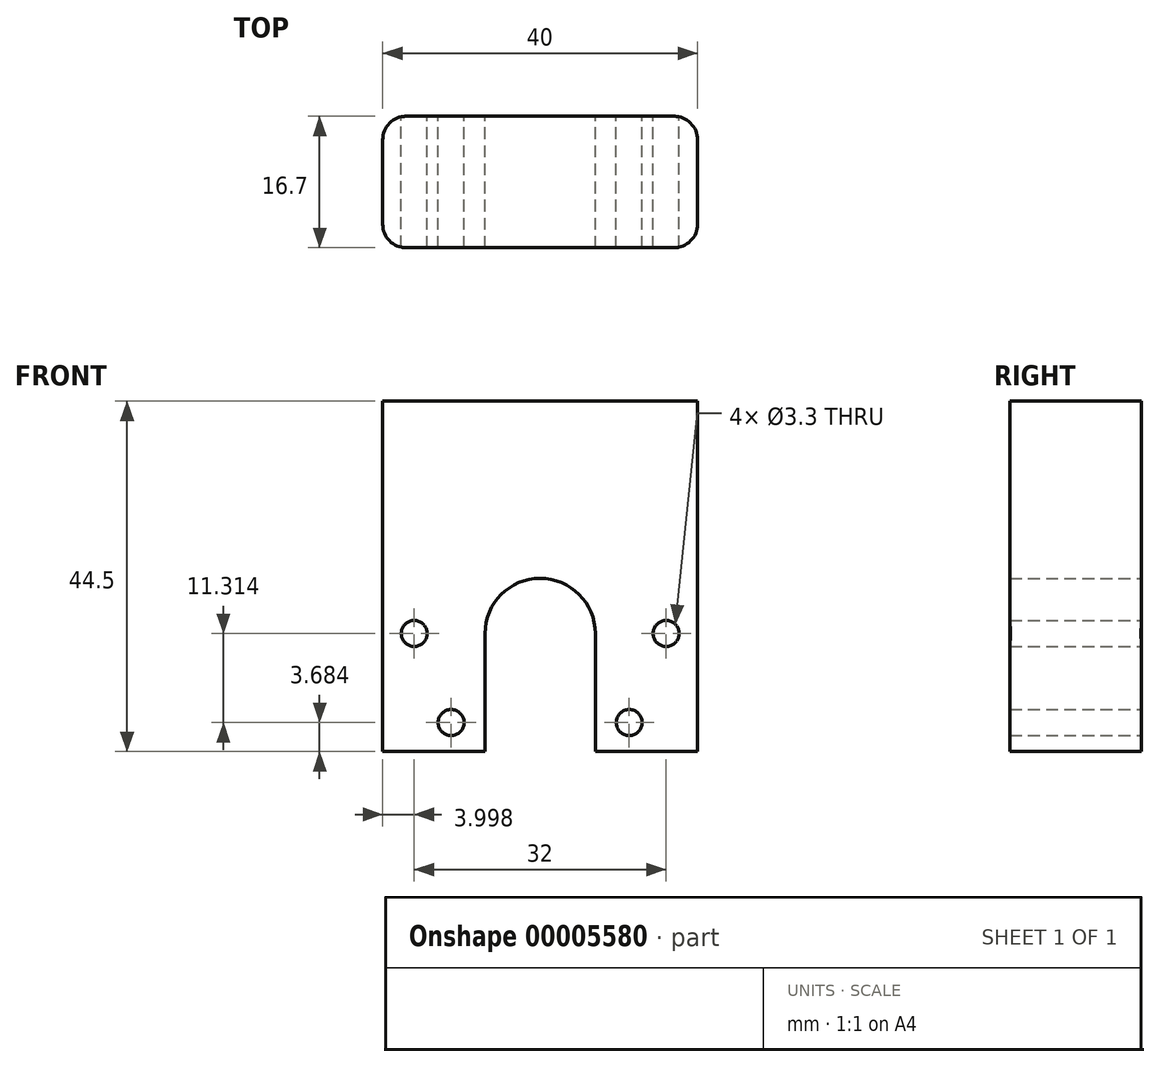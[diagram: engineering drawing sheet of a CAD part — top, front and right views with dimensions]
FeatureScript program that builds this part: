
annotation { "Feature Type Name" : "Feature", "Feature Type Description" : "" }
export const myFeature = defineFeature(function(context is Context, id is Id, definition is map)
    precondition{}
    {
        {
            var Q0;
            Q0=qCreatedBy(makeId("Front.planeOp"),FACE);
            var sketch = newSketch(context, id + "F0", { "sketchPlane" : qUnion([Q0])});
            skLineSegment(sketch, "E0.bottom", {"start": v(-19.28, 16.73) * mm, "end": v(20.72, 16.73) * mm});
            skLineSegment(sketch, "E0.top", {"start": v(-19.28, -27.77) * mm, "end": v(-6.28, -27.77) * mm});
            skLineSegment(sketch, "E0.left", {"start": v(-19.28, 16.73) * mm, "end": v(-19.28, -27.77) * mm});
            skLineSegment(sketch, "E0.right", {"start": v(20.72, 16.73) * mm, "end": v(20.72, -27.77) * mm});
            skLineSegment(sketch, "E1", {"start": v(0.72, 16.73) * mm, "end": v(0.72, -27.77) * mm, "construction": true});
            skLineSegment(sketch, "E2", {"start": v(0.72, -12.77) * mm, "end": v(-15.28, -12.77) * mm, "construction": true});
            skCircle(sketch, "E3", {"center": v(-15.28, -12.77) * mm, "radius": 1.65 * mm});
            skCircle(sketch, "E4.0.MirrorC", {"center": v(16.72, -12.77) * mm, "radius": 1.65 * mm});
            skArc(sketch, "E5", {"start": v(7.72, -12.77) * mm, "mid": v(0.72, -5.77) * mm, "end": v(-6.28, -12.77) * mm});
            skLineSegment(sketch, "E6", {"start": v(-6.28, -12.77) * mm, "end": v(-6.28, -27.77) * mm});
            skLineSegment(sketch, "E7", {"start": v(7.72, -12.77) * mm, "end": v(7.72, -27.77) * mm});
            skLineSegment(sketch, "E8.trimOffspring", {"start": v(7.72, -27.77) * mm, "end": v(20.72, -27.77) * mm});
            skLineSegment(sketch, "E9", {"start": v(0.72, -12.77) * mm, "end": v(0.72, 16.73) * mm, "construction": true});
            skLineSegment(sketch, "E10", {"start": v(20.72, -3.27) * mm, "end": v(-19.28, -3.27) * mm, "construction": true});
            skLineSegment(sketch, "E11", {"start": v(20.72, -4.77) * mm, "end": v(-19.28, -4.77) * mm, "construction": true});
            skCircle(sketch, "E12.1.0", {"center": v(-10.6, -24.09) * mm, "radius": 1.65 * mm});
            skLineSegment(sketch, "E12.anchor2", {"start": v(0.72, -12.77) * mm, "end": v(-10.6, -24.09) * mm, "construction": true});
            skCircle(sketch, "E13.0.MirrorC", {"center": v(12.03, -24.09) * mm, "radius": 1.65 * mm});
            skLineSegment(sketch, "E14", {"start": v(-9.88, -5.77) * mm, "end": v(14.62, -5.77) * mm, "construction": true});
            skSolve(sketch);
        }
        {
            var Q0;
            Q0 = qSketchRegion(id + "F0", true);
            extrude(context, id + "F1", {"entities" : qUnion([Q0]), "depth" : 16.7 * mm});
        }
        {
            var Q0;
            Q0=makeQuery(id+"F1.opExtrude","CAP_EDGE",EDGE,{"disambiguationData":[OSD([sQuery(id+"F0.wireOp",EDGE,"E0.left")])],"isStart":false});
            var Q1;
            Q1=makeQuery(id+"F1.opExtrude","CAP_EDGE",EDGE,{"disambiguationData":[OSD([sQuery(id+"F0.wireOp",EDGE,"E0.right")])],"isStart":false});
            var Q2;
            Q2=makeQuery(id+"F1.opExtrude","CAP_EDGE",EDGE,{"disambiguationData":[OSD([sQuery(id+"F0.wireOp",EDGE,"E0.right")])],"isStart":true});
            var Q3;
            Q3=makeQuery(id+"F1.opExtrude","CAP_EDGE",EDGE,{"disambiguationData":[OSD([sQuery(id+"F0.wireOp",EDGE,"E0.left")])],"isStart":true});
            fillet(context, id + "F2", {"entities" : qUnion([Q0, Q1, Q2, Q3]), "radius" : 3 * mm, "tangentPropagation" : true, "allowEdgeOverflow" : false});
        }
    });
